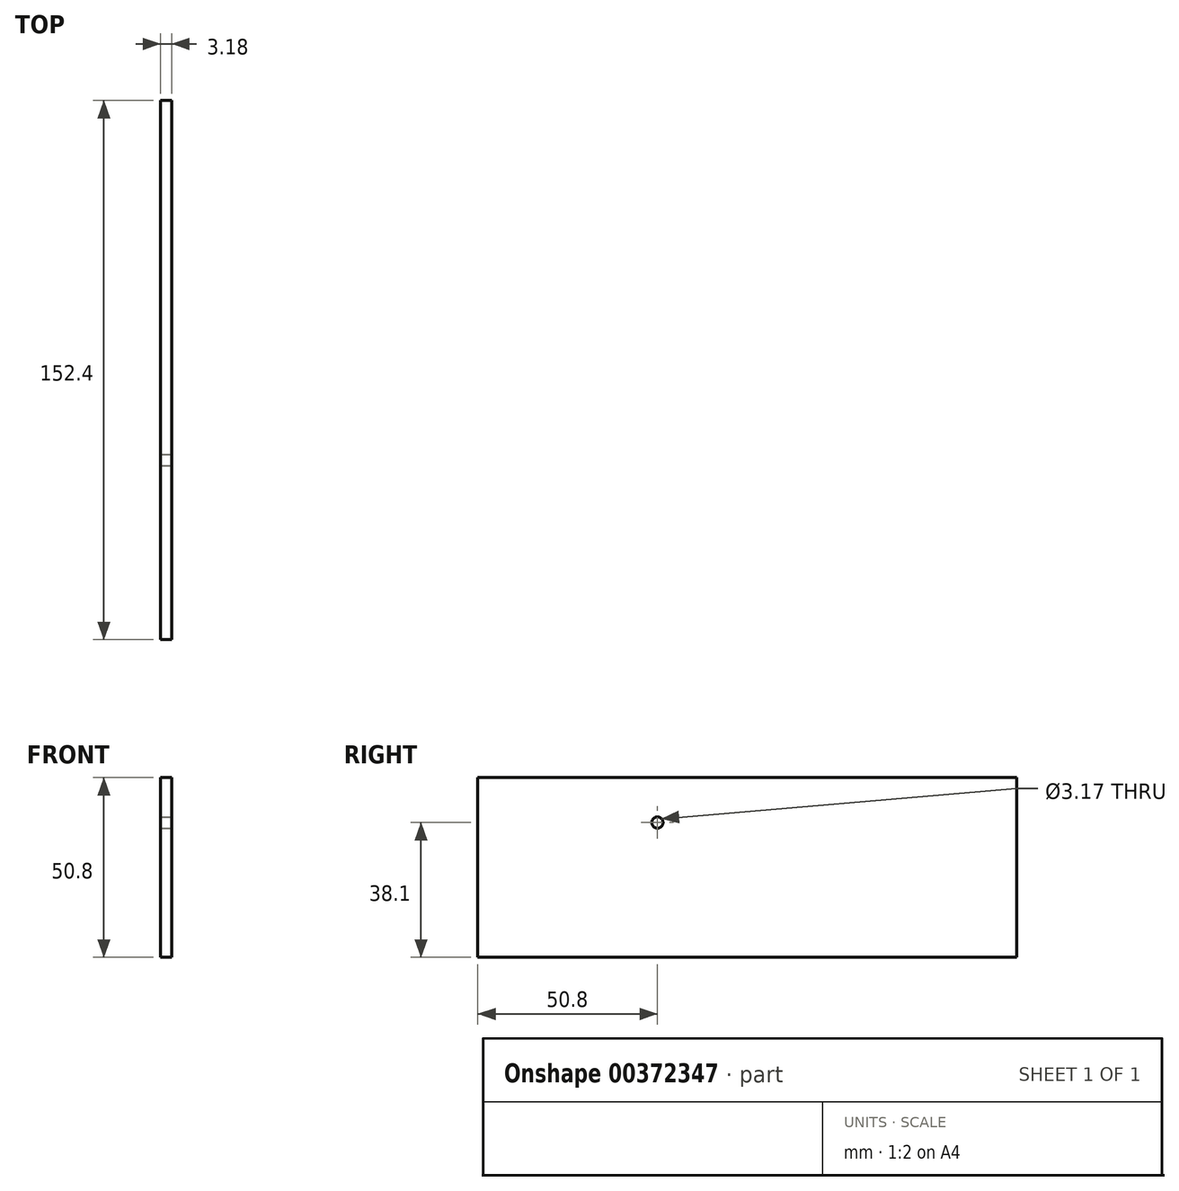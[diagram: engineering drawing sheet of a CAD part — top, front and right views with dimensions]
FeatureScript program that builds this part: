
annotation { "Feature Type Name" : "Feature", "Feature Type Description" : "" }
export const myFeature = defineFeature(function(context is Context, id is Id, definition is map)
    precondition{}
    {
        {
            var Q0;
            Q0=qCreatedBy(makeId("Right.planeOp"),FACE);
            var sketch = newSketch(context, id + "F0", { "sketchPlane" : qUnion([Q0])});
            skLineSegment(sketch, "E0.bottom", {"start": v(-76.2, 25.4) * mm, "end": v(76.2, 25.4) * mm});
            skLineSegment(sketch, "E0.top", {"start": v(-76.2, -25.4) * mm, "end": v(76.2, -25.4) * mm});
            skLineSegment(sketch, "E0.left", {"start": v(-76.2, 25.4) * mm, "end": v(-76.2, -25.4) * mm});
            skLineSegment(sketch, "E0.right", {"start": v(76.2, 25.4) * mm, "end": v(76.2, -25.4) * mm});
            skSolve(sketch);
        }
        {
            var Q0;
            Q0=qCreatedBy(makeId("Right.planeOp"),FACE);
            var sketch = newSketch(context, id + "F1", { "sketchPlane" : qUnion([Q0])});
            skCircle(sketch, "E1", {"center": v(-25.4, 12.7) * mm, "radius": 1.59 * mm});
            skSolve(sketch);
        }
        {
            var Q0;
            Q0 = qSketchRegion(id + "F0", true);
            extrude(context, id + "F2", {"entities" : qUnion([Q0]), "endBound" : BoundingType.SYMMETRIC, "depth" : 3.17 * mm});
        }
        {
            var Q0;
            Q0 = qSketchRegion(id + "F1", true);
            extrude(context, id + "F3", {"entities" : qUnion([Q0]), "operationType" : NewBodyOperationType.REMOVE, "endBound" : BoundingType.SYMMETRIC, "oppositeDirection" : true, "depth" : 3.17 * mm});
        }
    });
